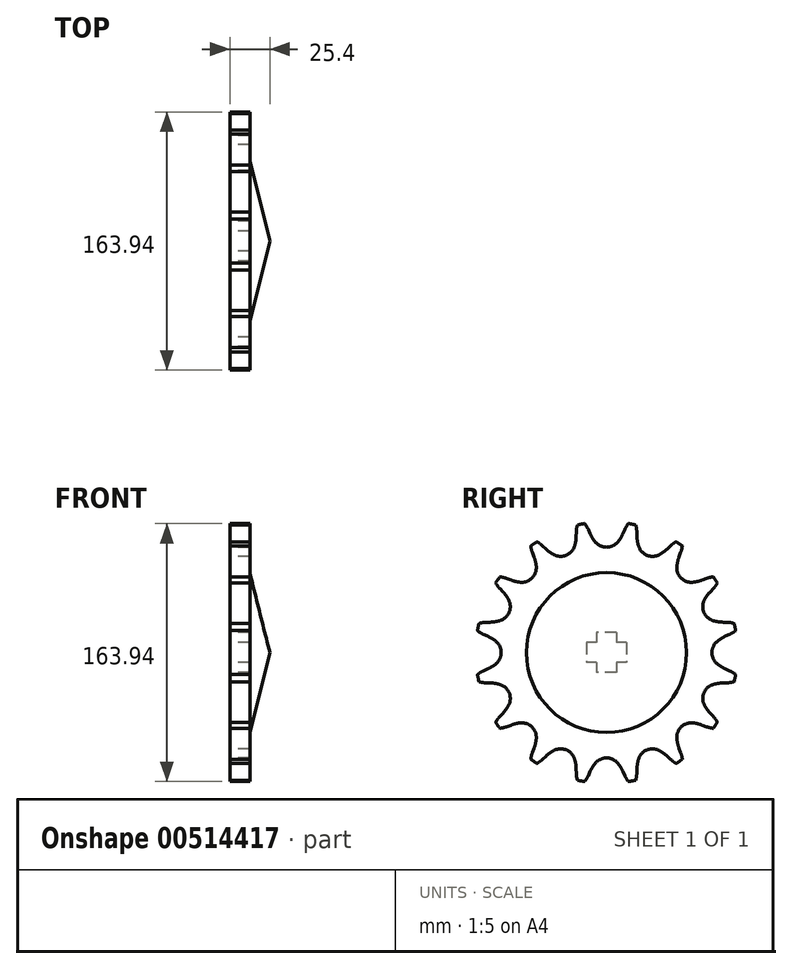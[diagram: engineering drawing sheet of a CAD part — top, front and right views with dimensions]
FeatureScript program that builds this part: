
annotation { "Feature Type Name" : "Feature", "Feature Type Description" : "" }
export const myFeature = defineFeature(function(context is Context, id is Id, definition is map)
    precondition{}
    {
        {
            var Q0;
            Q0=qCreatedBy(makeId("Front.planeOp"),FACE);
            var sketch = newSketch(context, id + "F0", { "sketchPlane" : qUnion([Q0])});
            skLineSegment(sketch, "E0", {"start": v(-32.2, 0) * mm, "end": v(32.68, 0) * mm, "construction": true});
            skLineSegment(sketch, "E1.bottom", {"start": v(-32.2, 25.4) * mm, "end": v(-19.5, 25.4) * mm});
            skLineSegment(sketch, "E1.top", {"start": v(-32.2, 88.9) * mm, "end": v(-19.5, 88.9) * mm});
            skLineSegment(sketch, "E1.left", {"start": v(-32.2, 25.4) * mm, "end": v(-32.2, 88.9) * mm});
            skLineSegment(sketch, "E1.right", {"start": v(-19.5, 25.4) * mm, "end": v(-19.5, 88.9) * mm});
            skLineSegment(sketch, "E2.MirrorCS", {"start": v(-19.5, -25.4) * mm, "end": v(-19.5, -88.9) * mm});
            skLineSegment(sketch, "E3.MirrorCS", {"start": v(-32.2, -25.4) * mm, "end": v(-32.2, -88.9) * mm});
            skLineSegment(sketch, "E4.MirrorCS", {"start": v(-32.2, -88.9) * mm, "end": v(-19.5, -88.9) * mm});
            skLineSegment(sketch, "E5.MirrorCS", {"start": v(-32.2, -25.4) * mm, "end": v(-19.5, -25.4) * mm});
            skLineSegment(sketch, "E6.bottom", {"start": v(-32.2, 50.8) * mm, "end": v(-6.8, 50.8) * mm});
            skLineSegment(sketch, "E6.top", {"start": v(-32.2, 25.4) * mm, "end": v(-6.8, 25.4) * mm});
            skLineSegment(sketch, "E6.left", {"start": v(-32.2, 50.8) * mm, "end": v(-32.2, 25.4) * mm});
            skLineSegment(sketch, "E6.right", {"start": v(-6.8, 50.8) * mm, "end": v(-6.8, 25.4) * mm});
            skLineSegment(sketch, "E7.MirrorCS", {"start": v(-6.8, -50.8) * mm, "end": v(-6.8, -25.4) * mm});
            skLineSegment(sketch, "E8.MirrorCS", {"start": v(-32.2, -50.8) * mm, "end": v(-32.2, -25.4) * mm});
            skLineSegment(sketch, "E9.MirrorCS", {"start": v(-32.2, -25.4) * mm, "end": v(-6.8, -25.4) * mm});
            skLineSegment(sketch, "E10.MirrorCS", {"start": v(-32.2, -50.8) * mm, "end": v(-6.8, -50.8) * mm});
            skSolve(sketch);
        }
        {
            var Q0;
            {var subQ5=sQuery(id+"F0.wireOp",EDGE,"E7.MirrorCS");Q0=makeQuery(id+"F0.imprint","IMPRINT",FACE,{"disambiguationData":[TD([[makeQuery(id+"F0.imprint","IMPRINT",EDGE,{"derivedFrom":subQ5}),1.0]])]});}
            var Q1;
            {var subQ5=sQuery(id+"F0.wireOp",EDGE,"E1.top");Q1=makeQuery(id+"F0.imprint","IMPRINT",FACE,{"disambiguationData":[TD([[makeQuery(id+"F0.imprint","IMPRINT",EDGE,{"derivedFrom":subQ5}),-1.0]])]});}
            var Q2;
            {var subQ4=sQuery(id+"F0.wireOp",EDGE,"E6.top");Q2=makeQuery(id+"F0.imprint","IMPRINT",FACE,{"disambiguationData":[TD([[makeQuery(id+"F0.imprint","IMPRINT",EDGE,{"derivedFrom":subQ4}),1.0]])]});}
            var Q3;
            {var subQ5=sQuery(id+"F0.wireOp",EDGE,"E8.MirrorCS");Q3=makeQuery(id+"F0.imprint","IMPRINT",FACE,{"disambiguationData":[TD([[makeQuery(id+"F0.imprint","IMPRINT",EDGE,{"derivedFrom":subQ5}),-1.0]])]});}
            var Q4;
            {var subQ5=sQuery(id+"F0.wireOp",EDGE,"E1.bottom");Q4=makeQuery(id+"F0.imprint","IMPRINT",FACE,{"disambiguationData":[TD([[makeQuery(id+"F0.imprint","IMPRINT",EDGE,{"derivedFrom":subQ5}),1.0]])]});}
            var Q5;
            {var subQ4=sQuery(id+"F0.wireOp",EDGE,"E3.MirrorCS");Q5=makeQuery(id+"F0.imprint","IMPRINT",FACE,{"disambiguationData":[TD([[makeQuery(id+"F0.imprint","IMPRINT",EDGE,{"derivedFrom":subQ4}),1.0]])]});}
            var Q6;
            Q6=sQuery(id+"F0.wireOp",EDGE,"E0");
            revolve(context, id + "F1", {"entities" : qUnion([Q0, Q1, Q2, Q3, Q4, Q5]), "axis" : qUnion([Q6]), "revolveType" : RevolveType.FULL});
        }
        {
            var Q0;
            Q0=makeQuery(id+"F1.opRevolve","SWEPT_FACE",FACE,{"disambiguationData":[OSD([sQuery(id+"F0.wireOp",EDGE,"E1.left")])]});
            var sketch = newSketch(context, id + "F2", { "sketchPlane" : qUnion([Q0])});
            skLineSegment(sketch, "E11", {"start": v(0, 0) * mm, "end": v(0, 76.2) * mm, "construction": true});
            skLineSegment(sketch, "E12", {"start": v(-10.43, 75.61) * mm, "end": v(-11.6, 78.21) * mm});
            skArc(sketch, "E13", {"start": v(-11.6, 78.21) * mm, "mid": v(-13.83, 81.86) * mm, "end": v(-16.88, 84.84) * mm});
            skLineSegment(sketch, "E14", {"start": v(-10.43, 75.61) * mm, "end": v(-10.43, 75.61) * mm});
            skArc(sketch, "E15", {"start": v(-10.43, 75.61) * mm, "mid": v(-9, 72.9) * mm, "end": v(-7.23, 70.4) * mm});
            skArc(sketch, "E16.MirrorCS", {"start": v(10.43, 75.61) * mm, "mid": v(9, 72.9) * mm, "end": v(7.23, 70.4) * mm});
            skArc(sketch, "E17.MirrorCS", {"start": v(11.6, 78.21) * mm, "mid": v(13.83, 81.86) * mm, "end": v(16.88, 84.84) * mm});
            skLineSegment(sketch, "E18.MirrorCS", {"start": v(10.43, 75.61) * mm, "end": v(11.6, 78.21) * mm});
            skArc(sketch, "E19", {"start": v(-7.23, 70.4) * mm, "mid": v(0, 66.92) * mm, "end": v(7.23, 70.4) * mm});
            skCircle(sketch, "E20.1.0", {"center": v(0, 0) * mm, "radius": 76.2 * mm, "construction": true});
            skArc(sketch, "E20.1.1", {"start": v(-40.65, 67.82) * mm, "mid": v(-44.1, 70.33) * mm, "end": v(-48.06, 71.92) * mm});
            skArc(sketch, "E20.1.2", {"start": v(-38.58, 65.87) * mm, "mid": v(-36.21, 63.9) * mm, "end": v(-33.62, 62.27) * mm});
            skLineSegment(sketch, "E20.1.3", {"start": v(-38.58, 65.87) * mm, "end": v(-40.65, 67.82) * mm});
            skArc(sketch, "E20.1.4", {"start": v(-33.62, 62.27) * mm, "mid": v(-25.61, 61.83) * mm, "end": v(-20.26, 67.8) * mm});
            skArc(sketch, "E20.1.5", {"start": v(-19.3, 73.85) * mm, "mid": v(-19.58, 70.8) * mm, "end": v(-20.26, 67.8) * mm});
            skLineSegment(sketch, "E20.1.6", {"start": v(-19.3, 73.85) * mm, "end": v(-19.21, 76.7) * mm});
            skArc(sketch, "E20.1.7", {"start": v(-19.21, 76.7) * mm, "mid": v(-18.55, 80.92) * mm, "end": v(-16.88, 84.84) * mm});
            skCircle(sketch, "E20.2.0", {"center": v(0, 0) * mm, "radius": 76.2 * mm, "construction": true});
            skArc(sketch, "E20.2.1", {"start": v(-63.5, 47.1) * mm, "mid": v(-67.66, 48.1) * mm, "end": v(-71.92, 48.06) * mm});
            skArc(sketch, "E20.2.2", {"start": v(-60.85, 46.1) * mm, "mid": v(-57.91, 45.19) * mm, "end": v(-54.9, 44.66) * mm});
            skLineSegment(sketch, "E20.2.3", {"start": v(-60.85, 46.1) * mm, "end": v(-63.5, 47.1) * mm});
            skArc(sketch, "E20.2.4", {"start": v(-54.9, 44.66) * mm, "mid": v(-47.32, 47.32) * mm, "end": v(-44.66, 54.9) * mm});
            skArc(sketch, "E20.2.5", {"start": v(-46.1, 60.85) * mm, "mid": v(-45.19, 57.91) * mm, "end": v(-44.66, 54.9) * mm});
            skLineSegment(sketch, "E20.2.6", {"start": v(-46.1, 60.85) * mm, "end": v(-47.1, 63.5) * mm});
            skArc(sketch, "E20.2.7", {"start": v(-47.1, 63.5) * mm, "mid": v(-48.1, 67.66) * mm, "end": v(-48.06, 71.92) * mm});
            skCircle(sketch, "E20.3.0", {"center": v(0, 0) * mm, "radius": 76.2 * mm, "construction": true});
            skArc(sketch, "E20.3.1", {"start": v(-76.7, 19.21) * mm, "mid": v(-80.92, 18.55) * mm, "end": v(-84.84, 16.88) * mm});
            skArc(sketch, "E20.3.2", {"start": v(-73.85, 19.3) * mm, "mid": v(-70.8, 19.58) * mm, "end": v(-67.8, 20.26) * mm});
            skLineSegment(sketch, "E20.3.3", {"start": v(-73.85, 19.3) * mm, "end": v(-76.7, 19.21) * mm});
            skArc(sketch, "E20.3.4", {"start": v(-67.8, 20.26) * mm, "mid": v(-61.83, 25.61) * mm, "end": v(-62.27, 33.62) * mm});
            skArc(sketch, "E20.3.5", {"start": v(-65.87, 38.58) * mm, "mid": v(-63.9, 36.21) * mm, "end": v(-62.27, 33.62) * mm});
            skLineSegment(sketch, "E20.3.6", {"start": v(-65.87, 38.58) * mm, "end": v(-67.82, 40.65) * mm});
            skArc(sketch, "E20.3.7", {"start": v(-67.82, 40.65) * mm, "mid": v(-70.33, 44.1) * mm, "end": v(-71.92, 48.06) * mm});
            skCircle(sketch, "E20.4.0", {"center": v(0, 0) * mm, "radius": 76.2 * mm, "construction": true});
            skArc(sketch, "E20.4.1", {"start": v(-78.21, -11.6) * mm, "mid": v(-81.86, -13.83) * mm, "end": v(-84.84, -16.88) * mm});
            skArc(sketch, "E20.4.2", {"start": v(-75.61, -10.43) * mm, "mid": v(-72.9, -9) * mm, "end": v(-70.4, -7.23) * mm});
            skLineSegment(sketch, "E20.4.3", {"start": v(-75.61, -10.43) * mm, "end": v(-78.21, -11.6) * mm});
            skArc(sketch, "E20.4.4", {"start": v(-70.4, -7.23) * mm, "mid": v(-66.92, 0) * mm, "end": v(-70.4, 7.23) * mm});
            skArc(sketch, "E20.4.5", {"start": v(-75.61, 10.43) * mm, "mid": v(-72.9, 9) * mm, "end": v(-70.4, 7.23) * mm});
            skLineSegment(sketch, "E20.4.6", {"start": v(-75.61, 10.43) * mm, "end": v(-78.21, 11.6) * mm});
            skArc(sketch, "E20.4.7", {"start": v(-78.21, 11.6) * mm, "mid": v(-81.86, 13.83) * mm, "end": v(-84.84, 16.88) * mm});
            skCircle(sketch, "E20.5.0", {"center": v(0, 0) * mm, "radius": 76.2 * mm, "construction": true});
            skArc(sketch, "E20.5.1", {"start": v(-67.82, -40.65) * mm, "mid": v(-70.33, -44.1) * mm, "end": v(-71.92, -48.06) * mm});
            skArc(sketch, "E20.5.2", {"start": v(-65.87, -38.58) * mm, "mid": v(-63.9, -36.21) * mm, "end": v(-62.27, -33.62) * mm});
            skLineSegment(sketch, "E20.5.3", {"start": v(-65.87, -38.58) * mm, "end": v(-67.82, -40.65) * mm});
            skArc(sketch, "E20.5.4", {"start": v(-62.27, -33.62) * mm, "mid": v(-61.83, -25.61) * mm, "end": v(-67.8, -20.26) * mm});
            skArc(sketch, "E20.5.5", {"start": v(-73.85, -19.3) * mm, "mid": v(-70.8, -19.58) * mm, "end": v(-67.8, -20.26) * mm});
            skLineSegment(sketch, "E20.5.6", {"start": v(-73.85, -19.3) * mm, "end": v(-76.7, -19.21) * mm});
            skArc(sketch, "E20.5.7", {"start": v(-76.7, -19.21) * mm, "mid": v(-80.92, -18.55) * mm, "end": v(-84.84, -16.88) * mm});
            skCircle(sketch, "E20.6.0", {"center": v(0, 0) * mm, "radius": 76.2 * mm, "construction": true});
            skArc(sketch, "E20.6.1", {"start": v(-47.1, -63.5) * mm, "mid": v(-48.1, -67.66) * mm, "end": v(-48.06, -71.92) * mm});
            skArc(sketch, "E20.6.2", {"start": v(-46.1, -60.85) * mm, "mid": v(-45.19, -57.91) * mm, "end": v(-44.66, -54.9) * mm});
            skLineSegment(sketch, "E20.6.3", {"start": v(-46.1, -60.85) * mm, "end": v(-47.1, -63.5) * mm});
            skArc(sketch, "E20.6.4", {"start": v(-44.66, -54.9) * mm, "mid": v(-47.32, -47.32) * mm, "end": v(-54.9, -44.66) * mm});
            skArc(sketch, "E20.6.5", {"start": v(-60.85, -46.1) * mm, "mid": v(-57.91, -45.19) * mm, "end": v(-54.9, -44.66) * mm});
            skLineSegment(sketch, "E20.6.6", {"start": v(-60.85, -46.1) * mm, "end": v(-63.5, -47.1) * mm});
            skArc(sketch, "E20.6.7", {"start": v(-63.5, -47.1) * mm, "mid": v(-67.66, -48.1) * mm, "end": v(-71.92, -48.06) * mm});
            skCircle(sketch, "E20.7.0", {"center": v(0, 0) * mm, "radius": 76.2 * mm, "construction": true});
            skArc(sketch, "E20.7.1", {"start": v(-19.21, -76.7) * mm, "mid": v(-18.55, -80.92) * mm, "end": v(-16.88, -84.84) * mm});
            skArc(sketch, "E20.7.2", {"start": v(-19.3, -73.85) * mm, "mid": v(-19.58, -70.8) * mm, "end": v(-20.26, -67.8) * mm});
            skLineSegment(sketch, "E20.7.3", {"start": v(-19.3, -73.85) * mm, "end": v(-19.21, -76.7) * mm});
            skArc(sketch, "E20.7.4", {"start": v(-20.26, -67.8) * mm, "mid": v(-25.61, -61.83) * mm, "end": v(-33.62, -62.27) * mm});
            skArc(sketch, "E20.7.5", {"start": v(-38.58, -65.87) * mm, "mid": v(-36.21, -63.9) * mm, "end": v(-33.62, -62.27) * mm});
            skLineSegment(sketch, "E20.7.6", {"start": v(-38.58, -65.87) * mm, "end": v(-40.65, -67.82) * mm});
            skArc(sketch, "E20.7.7", {"start": v(-40.65, -67.82) * mm, "mid": v(-44.1, -70.33) * mm, "end": v(-48.06, -71.92) * mm});
            skCircle(sketch, "E20.8.0", {"center": v(0, 0) * mm, "radius": 76.2 * mm, "construction": true});
            skArc(sketch, "E20.8.1", {"start": v(11.6, -78.21) * mm, "mid": v(13.83, -81.86) * mm, "end": v(16.88, -84.84) * mm});
            skArc(sketch, "E20.8.2", {"start": v(10.43, -75.61) * mm, "mid": v(9, -72.9) * mm, "end": v(7.23, -70.4) * mm});
            skLineSegment(sketch, "E20.8.3", {"start": v(10.43, -75.61) * mm, "end": v(11.6, -78.21) * mm});
            skArc(sketch, "E20.8.4", {"start": v(7.23, -70.4) * mm, "mid": v(0, -66.92) * mm, "end": v(-7.23, -70.4) * mm});
            skArc(sketch, "E20.8.5", {"start": v(-10.43, -75.61) * mm, "mid": v(-9, -72.9) * mm, "end": v(-7.23, -70.4) * mm});
            skLineSegment(sketch, "E20.8.6", {"start": v(-10.43, -75.61) * mm, "end": v(-11.6, -78.21) * mm});
            skArc(sketch, "E20.8.7", {"start": v(-11.6, -78.21) * mm, "mid": v(-13.83, -81.86) * mm, "end": v(-16.88, -84.84) * mm});
            skArc(sketch, "E20.9.1", {"start": v(40.65, -67.82) * mm, "mid": v(44.1, -70.33) * mm, "end": v(48.06, -71.92) * mm});
            skArc(sketch, "E20.9.2", {"start": v(38.58, -65.87) * mm, "mid": v(36.21, -63.9) * mm, "end": v(33.62, -62.27) * mm});
            skLineSegment(sketch, "E20.9.3", {"start": v(38.58, -65.87) * mm, "end": v(40.65, -67.82) * mm});
            skArc(sketch, "E20.9.4", {"start": v(33.62, -62.27) * mm, "mid": v(25.61, -61.83) * mm, "end": v(20.26, -67.8) * mm});
            skArc(sketch, "E20.9.5", {"start": v(19.3, -73.85) * mm, "mid": v(19.58, -70.8) * mm, "end": v(20.26, -67.8) * mm});
            skLineSegment(sketch, "E20.9.6", {"start": v(19.3, -73.85) * mm, "end": v(19.21, -76.7) * mm});
            skArc(sketch, "E20.9.7", {"start": v(19.21, -76.7) * mm, "mid": v(18.55, -80.92) * mm, "end": v(16.88, -84.84) * mm});
            skCircle(sketch, "E20.10.0", {"center": v(0, 0) * mm, "radius": 76.2 * mm, "construction": true});
            skArc(sketch, "E20.10.1", {"start": v(63.5, -47.1) * mm, "mid": v(67.66, -48.1) * mm, "end": v(71.92, -48.06) * mm});
            skArc(sketch, "E20.10.2", {"start": v(60.85, -46.1) * mm, "mid": v(57.91, -45.19) * mm, "end": v(54.9, -44.66) * mm});
            skLineSegment(sketch, "E20.10.3", {"start": v(60.85, -46.1) * mm, "end": v(63.5, -47.1) * mm});
            skArc(sketch, "E20.10.4", {"start": v(54.9, -44.66) * mm, "mid": v(47.32, -47.32) * mm, "end": v(44.66, -54.9) * mm});
            skArc(sketch, "E20.10.5", {"start": v(46.1, -60.85) * mm, "mid": v(45.19, -57.91) * mm, "end": v(44.66, -54.9) * mm});
            skLineSegment(sketch, "E20.10.6", {"start": v(46.1, -60.85) * mm, "end": v(47.1, -63.5) * mm});
            skArc(sketch, "E20.10.7", {"start": v(47.1, -63.5) * mm, "mid": v(48.1, -67.66) * mm, "end": v(48.06, -71.92) * mm});
            skCircle(sketch, "E20.11.0", {"center": v(0, 0) * mm, "radius": 76.2 * mm, "construction": true});
            skArc(sketch, "E20.11.1", {"start": v(76.7, -19.21) * mm, "mid": v(80.92, -18.55) * mm, "end": v(84.84, -16.88) * mm});
            skArc(sketch, "E20.11.2", {"start": v(73.85, -19.3) * mm, "mid": v(70.8, -19.58) * mm, "end": v(67.8, -20.26) * mm});
            skLineSegment(sketch, "E20.11.3", {"start": v(73.85, -19.3) * mm, "end": v(76.7, -19.21) * mm});
            skArc(sketch, "E20.11.4", {"start": v(67.8, -20.26) * mm, "mid": v(61.83, -25.61) * mm, "end": v(62.27, -33.62) * mm});
            skArc(sketch, "E20.11.5", {"start": v(65.87, -38.58) * mm, "mid": v(63.9, -36.21) * mm, "end": v(62.27, -33.62) * mm});
            skLineSegment(sketch, "E20.11.6", {"start": v(65.87, -38.58) * mm, "end": v(67.82, -40.65) * mm});
            skArc(sketch, "E20.11.7", {"start": v(67.82, -40.65) * mm, "mid": v(70.33, -44.1) * mm, "end": v(71.92, -48.06) * mm});
            skCircle(sketch, "E20.12.0", {"center": v(0, 0) * mm, "radius": 76.2 * mm, "construction": true});
            skArc(sketch, "E20.12.1", {"start": v(78.21, 11.6) * mm, "mid": v(81.86, 13.83) * mm, "end": v(84.84, 16.88) * mm});
            skArc(sketch, "E20.12.2", {"start": v(75.61, 10.43) * mm, "mid": v(72.9, 9) * mm, "end": v(70.4, 7.23) * mm});
            skLineSegment(sketch, "E20.12.3", {"start": v(75.61, 10.43) * mm, "end": v(78.21, 11.6) * mm});
            skArc(sketch, "E20.12.4", {"start": v(70.4, 7.23) * mm, "mid": v(66.92, 0) * mm, "end": v(70.4, -7.23) * mm});
            skArc(sketch, "E20.12.5", {"start": v(75.61, -10.43) * mm, "mid": v(72.9, -9) * mm, "end": v(70.4, -7.23) * mm});
            skLineSegment(sketch, "E20.12.6", {"start": v(75.61, -10.43) * mm, "end": v(78.21, -11.6) * mm});
            skArc(sketch, "E20.12.7", {"start": v(78.21, -11.6) * mm, "mid": v(81.86, -13.83) * mm, "end": v(84.84, -16.88) * mm});
            skCircle(sketch, "E20.13.0", {"center": v(0, 0) * mm, "radius": 76.2 * mm, "construction": true});
            skArc(sketch, "E20.13.1", {"start": v(67.82, 40.65) * mm, "mid": v(70.33, 44.1) * mm, "end": v(71.92, 48.06) * mm});
            skArc(sketch, "E20.13.2", {"start": v(65.87, 38.58) * mm, "mid": v(63.9, 36.21) * mm, "end": v(62.27, 33.62) * mm});
            skLineSegment(sketch, "E20.13.3", {"start": v(65.87, 38.58) * mm, "end": v(67.82, 40.65) * mm});
            skArc(sketch, "E20.13.4", {"start": v(62.27, 33.62) * mm, "mid": v(61.83, 25.61) * mm, "end": v(67.8, 20.26) * mm});
            skArc(sketch, "E20.13.5", {"start": v(73.85, 19.3) * mm, "mid": v(70.8, 19.58) * mm, "end": v(67.8, 20.26) * mm});
            skLineSegment(sketch, "E20.13.6", {"start": v(73.85, 19.3) * mm, "end": v(76.7, 19.21) * mm});
            skArc(sketch, "E20.13.7", {"start": v(76.7, 19.21) * mm, "mid": v(80.92, 18.55) * mm, "end": v(84.84, 16.88) * mm});
            skCircle(sketch, "E20.14.0", {"center": v(0, 0) * mm, "radius": 76.2 * mm, "construction": true});
            skArc(sketch, "E20.14.1", {"start": v(47.1, 63.5) * mm, "mid": v(48.1, 67.66) * mm, "end": v(48.06, 71.92) * mm});
            skArc(sketch, "E20.14.2", {"start": v(46.1, 60.85) * mm, "mid": v(45.19, 57.91) * mm, "end": v(44.66, 54.9) * mm});
            skLineSegment(sketch, "E20.14.3", {"start": v(46.1, 60.85) * mm, "end": v(47.1, 63.5) * mm});
            skArc(sketch, "E20.14.4", {"start": v(44.66, 54.9) * mm, "mid": v(47.32, 47.32) * mm, "end": v(54.9, 44.66) * mm});
            skArc(sketch, "E20.14.5", {"start": v(60.85, 46.1) * mm, "mid": v(57.91, 45.19) * mm, "end": v(54.9, 44.66) * mm});
            skLineSegment(sketch, "E20.14.6", {"start": v(60.85, 46.1) * mm, "end": v(63.5, 47.1) * mm});
            skArc(sketch, "E20.14.7", {"start": v(63.5, 47.1) * mm, "mid": v(67.66, 48.1) * mm, "end": v(71.92, 48.06) * mm});
            skCircle(sketch, "E20.15.0", {"center": v(0, 0) * mm, "radius": 76.2 * mm, "construction": true});
            skArc(sketch, "E20.15.1", {"start": v(19.21, 76.7) * mm, "mid": v(18.55, 80.92) * mm, "end": v(16.88, 84.84) * mm});
            skArc(sketch, "E20.15.2", {"start": v(19.3, 73.85) * mm, "mid": v(19.58, 70.8) * mm, "end": v(20.26, 67.8) * mm});
            skLineSegment(sketch, "E20.15.3", {"start": v(19.3, 73.85) * mm, "end": v(19.21, 76.7) * mm});
            skArc(sketch, "E20.15.4", {"start": v(20.26, 67.8) * mm, "mid": v(25.61, 61.83) * mm, "end": v(33.62, 62.27) * mm});
            skArc(sketch, "E20.15.5", {"start": v(38.58, 65.87) * mm, "mid": v(36.21, 63.9) * mm, "end": v(33.62, 62.27) * mm});
            skLineSegment(sketch, "E20.15.6", {"start": v(38.58, 65.87) * mm, "end": v(40.65, 67.82) * mm});
            skArc(sketch, "E20.15.7", {"start": v(40.65, 67.82) * mm, "mid": v(44.1, 70.33) * mm, "end": v(48.06, 71.92) * mm});
            skPoint(sketch, "E20.center", {"position": v(0, 0) * mm});
            skCircle(sketch, "E21", {"center": v(0, 0) * mm, "radius": 83.14 * mm});
            skPoint(sketch, "E22", {"position": v(141.06, -0.1) * mm});
            skSolve(sketch);
        }
        {
            var Q0;
            {var subQ50=sQuery(id+"F2.wireOp",EDGE,"E12");Q0=makeQuery(id+"F2.imprint","IMPRINT",FACE,{"disambiguationData":[TD([[makeQuery(id+"F2.imprint","IMPRINT",EDGE,{"derivedFrom":subQ50}),1.0]])]});}
            extrude(context, id + "F3", {"entities" : qUnion([Q0]), "operationType" : NewBodyOperationType.INTERSECT, "endBound" : BoundingType.THROUGH_ALL, "oppositeDirection" : true, "depth" : 25.4 * mm, "offsetDistance" : 25.4 * mm});
        }
        {
            var Q0;
            Q0=makeQuery(id+"F1.opRevolve","SWEPT_FACE",FACE,{"disambiguationData":[OSD([sQuery(id+"F0.wireOp",EDGE,"E6.right")])]});
            var sketch = newSketch(context, id + "F4", { "sketchPlane" : qUnion([Q0])});
            skCircle(sketch, "E23", {"center": v(0, 0) * mm, "radius": 25.4 * mm});
            skSolve(sketch);
        }
        {
            var Q0;
            Q0=makeQuery(id+"F4.imprint","IMPRINT",FACE,{"disambiguationData":[TD([[makeQuery(id+"F4.imprint","IMPRINT",EDGE,{"derivedFrom":sQuery(id+"F4.wireOp",EDGE,"E23")}),-1.0]])]});
            extrude(context, id + "F5", {"entities" : qUnion([Q0]), "operationType" : NewBodyOperationType.ADD, "oppositeDirection" : true, "depth" : 12.7 * mm, "offsetDistance" : 25.4 * mm});
        }
        {
            var Q0;
            Q0=makeQuery(id+"F1.opRevolve","SWEPT_FACE",FACE,{"disambiguationData":[OSD([sQuery(id+"F0.wireOp",EDGE,"E1.left")])]});
            var sketch = newSketch(context, id + "F6", { "sketchPlane" : qUnion([Q0])});
            skCircle(sketch, "E24", {"center": v(0, 0) * mm, "radius": 25.4 * mm});
            skLineSegment(sketch, "E25.bottom", {"start": v(-12.7, 6.35) * mm, "end": v(12.7, 6.35) * mm});
            skLineSegment(sketch, "E25.top", {"start": v(-12.7, -6.35) * mm, "end": v(12.7, -6.35) * mm});
            skLineSegment(sketch, "E25.left", {"start": v(-12.7, 6.35) * mm, "end": v(-12.7, -6.35) * mm});
            skLineSegment(sketch, "E25.right", {"start": v(12.7, 6.35) * mm, "end": v(12.7, -6.35) * mm});
            skLineSegment(sketch, "E26.bottom", {"start": v(-6.35, 12.7) * mm, "end": v(6.35, 12.7) * mm});
            skLineSegment(sketch, "E26.top", {"start": v(-6.35, -12.7) * mm, "end": v(6.35, -12.7) * mm});
            skLineSegment(sketch, "E26.left", {"start": v(-6.35, 12.7) * mm, "end": v(-6.35, -12.7) * mm});
            skLineSegment(sketch, "E26.right", {"start": v(6.35, 12.7) * mm, "end": v(6.35, -12.7) * mm});
            skSolve(sketch);
        }
        {
            var Q0;
            Q0=makeQuery(id+"F6.imprint","IMPRINT",FACE,{"disambiguationData":[TD([[makeQuery(id+"F6.imprint","IMPRINT",EDGE,{"derivedFrom":sQuery(id+"F6.wireOp",EDGE,"E24")}),1.0]])]});
            extrude(context, id + "F7", {"entities" : qUnion([Q0]), "operationType" : NewBodyOperationType.ADD, "oppositeDirection" : true, "depth" : 12.7 * mm, "offsetDistance" : 25.4 * mm});
        }
        {
            var Q0;
            Q0=makeQuery(id+"F1.opRevolve","SWEPT_EDGE",EDGE,{"disambiguationData":[OSD([sQuery(id+"F0.wireOp",EDGE,"E6.bottom"),sQuery(id+"F0.wireOp",EDGE,"E6.right")])]});
            chamfer(context, id + "F8", {"entities" : qUnion([Q0]), "chamferType" : ChamferType.TWO_OFFSETS, "width1" : 12.7 * mm, "oppositeDirection" : false, "width2" : 50.8 * mm, "tangentPropagation" : true});
        }
    });
